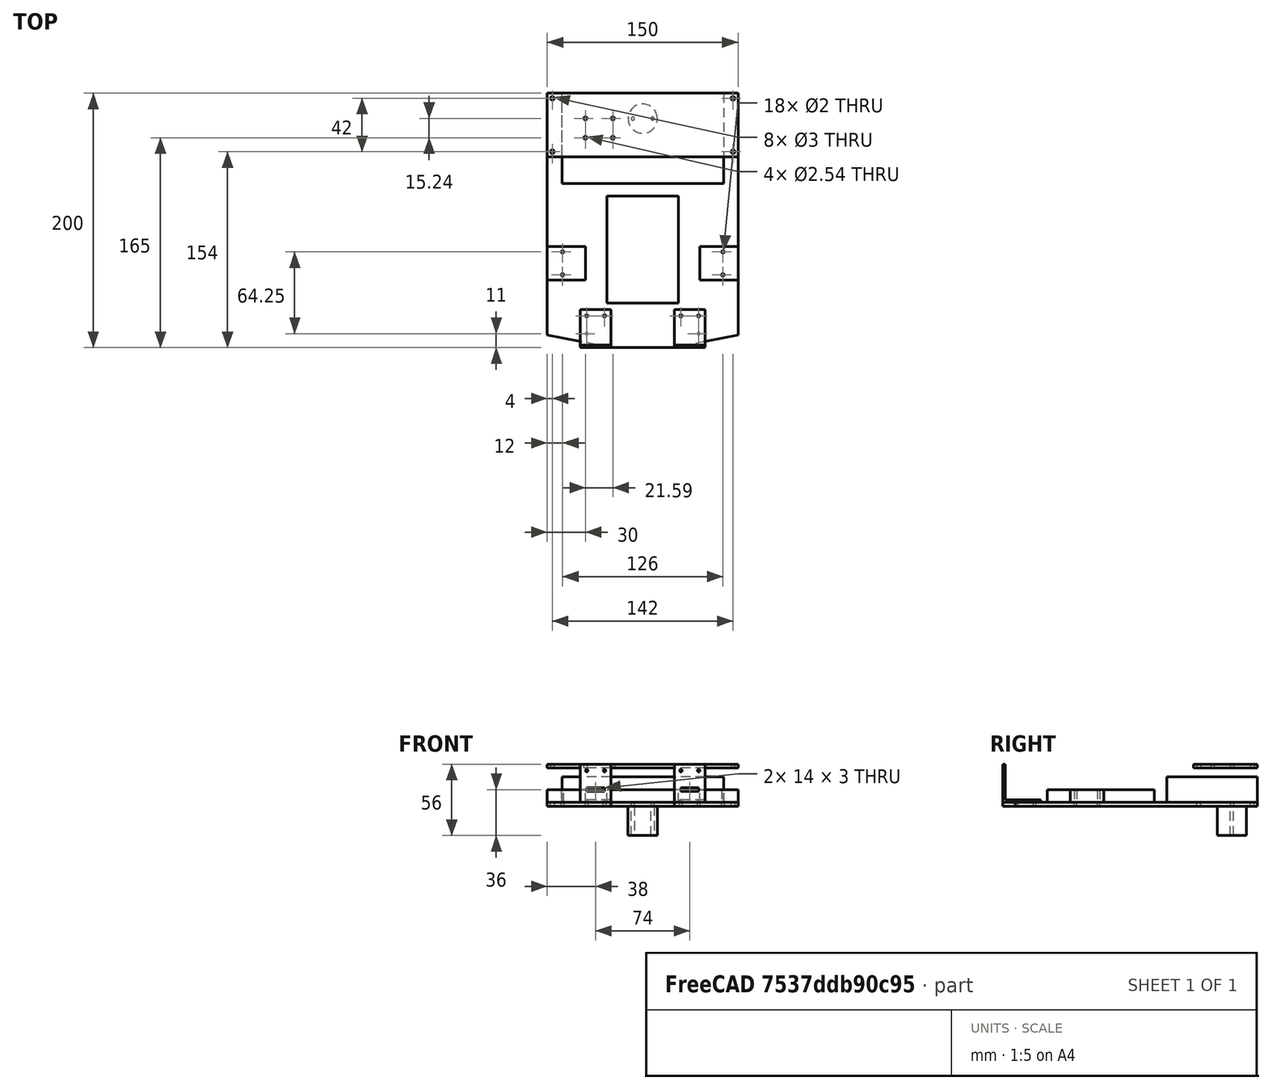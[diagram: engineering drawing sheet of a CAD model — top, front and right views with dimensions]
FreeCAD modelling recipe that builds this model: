
FCSTD DOCUMENT  (FreeCAD 0.20R29177 (Git))
Label: robot
License: All rights reserved
LicenseURL: http://en.wikipedia.org/wiki/All_rights_reserved
objects: TechDraw::DrawViewDimension×62, PartDesign::ShapeBinder×18, PartDesign::Pocket×13, PartDesign::Pad×11, PartDesign::Body×10, TechDraw::DrawProjGroupItem×10, Sketcher::SketchObject×9, TechDraw::DrawSVGTemplate×8, TechDraw::DrawPage×8, TechDraw::DrawProjGroup×7, PartDesign::SubShapeBinder×6, TechDraw::DrawViewAnnotation×3, PartDesign::Fillet×2, App::Part×1
note: 95 computed .brp shape members not serialized (recipe doc carries the construction recipe); baked Part::Feature solids carry a one-line shape summary decoded from their .brp

FEATURE [Sketcher::SketchObject] Sketch  label="ChassisOutline"
  FullyConstrained = true
  MapMode = 5
  Support = -> [XY_Plane]
  sketch-geometry (4):
    g0: LineSegment StartX=-75 StartY=100 StartZ=0 EndX=75 EndY=100 EndZ=0
    g1: LineSegment StartX=75 StartY=100 StartZ=0 EndX=75 EndY=-100 EndZ=0
    g2: LineSegment StartX=75 StartY=-100 StartZ=0 EndX=-75 EndY=-100 EndZ=0
    g3: LineSegment StartX=-75 StartY=-100 StartZ=0 EndX=-75 EndY=100 EndZ=0
  constraints (11):
    c: Coincident(g0,g1)
    c: Coincident(g3,g0)
    c: Horizontal(g0)
    c: Vertical(g1)
    c: Vertical(g3)
    c: Distance(g0) = 150
    c: DistanceY(g2,g0) = 200
    c: Coincident(g2,g1)
    c: Coincident(g2,g3)
    c: Symmetric(g1,g0,g-1)
    c: Horizontal(g2)
FEATURE [Sketcher::SketchObject] Sketch001  label="UpperParts"
  AttachmentOffset = pos=(0,0,3) rot=(0,0,1;0rad)
  ExternalGeometry = -> [Sketch]
  FullyConstrained = true
  MapMode = 5
  Placement = pos=(0,0,3) rot=(0,0,1;0rad)
  Support = -> [XY_Plane]
  sketch-geometry (21):
    g0: LineSegment StartX=-63.5 StartY=100 StartZ=0 EndX=63.5 EndY=100 EndZ=0
    g1: LineSegment StartX=63.5 StartY=100 StartZ=0 EndX=63.5 EndY=29 EndZ=0
    g2: LineSegment StartX=63.5 StartY=29 StartZ=0 EndX=-63.5 EndY=29 EndZ=0
    g3: LineSegment StartX=-63.5 StartY=29 StartZ=0 EndX=-63.5 EndY=100 EndZ=0
    g4: LineSegment StartX=-28 StartY=19 StartZ=0 EndX=28 EndY=19 EndZ=0
    g5: LineSegment StartX=28 StartY=19 StartZ=0 EndX=28 EndY=-65 EndZ=0
    g6: LineSegment StartX=28 StartY=-65 StartZ=0 EndX=-28 EndY=-65 EndZ=0
    g7: LineSegment StartX=-28 StartY=-65 StartZ=0 EndX=-28 EndY=19 EndZ=0
    g8: LineSegment StartX=-75 StartY=-47 StartZ=0 EndX=-45 EndY=-47 EndZ=0
    g9: LineSegment StartX=-45 StartY=-47 StartZ=0 EndX=-45 EndY=-20.5 EndZ=0
    g10: LineSegment StartX=-45 StartY=-20.5 StartZ=0 EndX=-75 EndY=-20.5 EndZ=0
    g11: LineSegment StartX=-75 StartY=-20.5 StartZ=0 EndX=-75 EndY=-47 EndZ=0
    g12: LineSegment StartX=75 StartY=-20.5 StartZ=0 EndX=45 EndY=-20.5 EndZ=0
    g13: LineSegment StartX=45 StartY=-20.5 StartZ=0 EndX=45 EndY=-47 EndZ=0
    g14: LineSegment StartX=45 StartY=-47 StartZ=0 EndX=75 EndY=-47 EndZ=0
    g15: LineSegment StartX=75 StartY=-47 StartZ=0 EndX=75 EndY=-20.5 EndZ=0
    g16: Circle CenterX=-63 CenterY=-24.75 CenterZ=0 NormalX=0 NormalY=0 NormalZ=1 AngleXU=0 Radius=1
    g17: Circle CenterX=-63 CenterY=-42.75 CenterZ=0 NormalX=0 NormalY=0 NormalZ=1 AngleXU=0 Radius=1
    g18: Circle CenterX=63 CenterY=-24.75 CenterZ=0 NormalX=0 NormalY=0 NormalZ=1 AngleXU=0 Radius=1
    g19: Circle CenterX=63 CenterY=-42.75 CenterZ=0 NormalX=0 NormalY=0 NormalZ=1 AngleXU=0 Radius=1
    g20: LineSegment StartX=-45 StartY=-33.75 StartZ=0 EndX=-75 EndY=-33.75 EndZ=0
  constraints (57):
    c: Coincident(g0,g1)
    c: Coincident(g1,g2)
    c: Coincident(g2,g3)
    c: Coincident(g3,g0)
    c: Horizontal(g0)
    c: Vertical(g1)
    c: Vertical(g3)
    c: PointOnObject(g0,g-3)
    c: Coincident(g4,g5)
    c: Coincident(g5,g6)
    c: Coincident(g6,g7)
    c: Coincident(g7,g4)
    c: Horizontal(g6)
    c: Vertical(g5)
    c: Vertical(g7)
    c: Distance(g3) = 71
    c: Distance(g2) = 127
    c: Distance(g6) = 56
    c: Distance(g5) = 84
    c: DistanceY(g4,g2) = 10
    c: Symmetric(g2,g1,g-2)
    c: Symmetric(g4,g4,g-2)
    c: Coincident(g8,g9)
    c: Coincident(g9,g10)
    c: Coincident(g10,g11)
    c: Coincident(g11,g8)
    c: Horizontal(g8)
    c: Horizontal(g10)
    c: Vertical(g9)
    c: Vertical(g11)
    c: PointOnObject(g8,g-4)
    c: Coincident(g12,g13)
    c: Coincident(g13,g14)
    c: Coincident(g14,g15)
    c: Coincident(g15,g12)
    c: Horizontal(g12)
    c: Horizontal(g14)
    c: Vertical(g13)
    c: Vertical(g15)
    c: PointOnObject(g12,g-5)
    c: Equal(g13,g9)
    c: Symmetric(g9,g12,g-2)
    c: DistanceX(g10,g10) = 30
    c: DistanceY(g11,g11) = 26.5
    c: PointOnObject(g20,g9)
    c: PointOnObject(g20,g11)
    c: Symmetric(g10,g8,g20)
    c: Symmetric(g16,g17,g20)
    c: Symmetric(g16,g18,g-2)
    c: Equal(g18,g19)
    c: Equal(g19,g17)
    c: Equal(g17,g16)
    c: Diameter(g16) = 2
    c: DistanceX(g20,g16) = 12
    c: Symmetric(g19,g17,g-2)
    c: DistanceY(g17,g16) = 18
    c: DistanceY(g6,g8) = 18
FEATURE [Sketcher::SketchObject] Sketch002  label="LowerParts"
  ExternalGeometry = -> [Sketch]
  FullyConstrained = true
  MapMode = 5
  Support = -> [XY_Plane]
  sketch-geometry (3):
    g0: Circle CenterX=0 CenterY=80 CenterZ=0 NormalX=0 NormalY=0 NormalZ=1 AngleXU=0 Radius=11.5
    g1: Circle CenterX=-7.75 CenterY=80 CenterZ=0 NormalX=0 NormalY=0 NormalZ=1 AngleXU=0 Radius=1.25
    g2: Circle CenterX=7.75 CenterY=80 CenterZ=0 NormalX=0 NormalY=0 NormalZ=1 AngleXU=0 Radius=1.25
  constraints (8):
    c: PointOnObject(g0,g-2)
    c: Symmetric(g1,g2,g-2)
    c: Horizontal(g0,g1)
    c: Diameter(g2) = 2.5
    c: Equal(g2,g1)
    c: Diameter(g0) = 23
    c: DistanceX(g1,g2) = 15.5
    c: DistanceY(g0,g-3) = 20
FEATURE [PartDesign::ShapeBinder] ShapeBinder
  Support = -> [Sketch,Sketch002,Sketch001]
  TraceSupport = false
FEATURE [PartDesign::Pad] Pad
  Direction = (0,0,1)
  Length = 3
  Length2 = 10
  Profile = -> ShapeBinder
  Type = 0
FEATURE [PartDesign::ShapeBinder] ShapeBinder001
  Support = -> [Sketch001]
  TraceSupport = false
FEATURE [PartDesign::Pocket] Pocket
  BaseFeature = -> Pad
  Direction = (0,0,-1)
  Length = 5
  Length2 = 5
  Profile = -> ShapeBinder001
  Type = 1
FEATURE [PartDesign::ShapeBinder] ShapeBinder002
  Support = -> [Sketch001]
  TraceSupport = false
FEATURE [PartDesign::Pad] Pad001
  Direction = (0,0,1)
  Length = 20
  Length2 = 10
  Profile = -> ShapeBinder002
  Type = 0
FEATURE [PartDesign::Body] Body002  label="BatteryBox"
  Group = -> [ShapeBinder002,Pad001]
  Origin = -> Origin002
  Tip = -> Pad001
FEATURE [PartDesign::ShapeBinder] ShapeBinder003
  Support = -> [Sketch001]
  TraceSupport = false
FEATURE [PartDesign::Pad] Pad002
  Direction = (0,0,1)
  Length = 10
  Length2 = 10
  Profile = -> ShapeBinder003
  Type = 0
FEATURE [PartDesign::Body] Body003  label="Breadboard"
  Group = -> [ShapeBinder003,Pad002]
  Origin = -> Origin003
  Tip = -> Pad002
FEATURE [PartDesign::ShapeBinder] ShapeBinder004
  Support = -> [Sketch001]
  TraceSupport = false
FEATURE [PartDesign::Pad] Pad003
  Direction = (0,0,1)
  Length = 10
  Length2 = 10
  Profile = -> ShapeBinder004
  Type = 0
FEATURE [PartDesign::Body] Body004  label="LeftMotor"
  Group = -> [ShapeBinder004,Pad003]
  Origin = -> Origin004
  Tip = -> Pad003
FEATURE [PartDesign::ShapeBinder] ShapeBinder005
  Support = -> [Sketch001]
  TraceSupport = false
FEATURE [PartDesign::Pad] Pad004
  Direction = (0,0,1)
  Length = 10
  Length2 = 10
  Profile = -> ShapeBinder005
  Type = 0
FEATURE [PartDesign::Body] Body005  label="RightMotor"
  Group = -> [ShapeBinder005,Pad004]
  Origin = -> Origin005
  Tip = -> Pad004
FEATURE [PartDesign::ShapeBinder] ShapeBinder006
  Support = -> [Sketch001]
  TraceSupport = false
FEATURE [PartDesign::Pocket] Pocket001
  BaseFeature = -> Pocket
  Direction = (0,0,-1)
  Length = 5
  Length2 = 5
  Profile = -> ShapeBinder006
  Type = 1
FEATURE [PartDesign::ShapeBinder] ShapeBinder007
  Support = -> [Sketch002]
  TraceSupport = false
FEATURE [PartDesign::Pocket] Pocket002
  BaseFeature = -> Pocket001
  Direction = (0,0,-1)
  Length = 5
  Length2 = 5
  Profile = -> ShapeBinder007
  Reversed = true
  Type = 1
FEATURE [PartDesign::ShapeBinder] ShapeBinder008
  Support = -> [Sketch002]
  TraceSupport = false
FEATURE [PartDesign::Pad] Pad005
  Direction = (0,0,1)
  Length = 23
  Length2 = 10
  Profile = -> ShapeBinder008
  Reversed = true
  Type = 0
FEATURE [PartDesign::Body] Body006  label="Castor"
  Group = -> [ShapeBinder008,Pad005]
  Origin = -> Origin006
  Tip = -> Pad005
FEATURE [TechDraw::DrawSVGTemplate] Template
  Height = 297
  Orientation = 0
  Width = 210
FEATURE [Sketcher::SketchObject] Sketch003  label="BevelFront"
  ExternalGeometry = -> [Sketch]
  FullyConstrained = true
  MapMode = 5
  Support = -> [XY_Plane]
  sketch-geometry (6):
    g0: LineSegment StartX=-75 StartY=-90 StartZ=0 EndX=-25 EndY=-100 EndZ=0
    g1: LineSegment StartX=25 StartY=-100 StartZ=0 EndX=75 EndY=-90 EndZ=0
    g2: LineSegment StartX=-75 StartY=-90 StartZ=0 EndX=-75 EndY=-100 EndZ=0
    g3: LineSegment StartX=-25 StartY=-100 StartZ=0 EndX=-75 EndY=-100 EndZ=0
    g4: LineSegment StartX=25 StartY=-100 StartZ=0 EndX=75 EndY=-100 EndZ=0
    g5: LineSegment StartX=75 StartY=-100 StartZ=0 EndX=75 EndY=-90 EndZ=0
  constraints (14):
    c: PointOnObject(g0,g-4)
    c: PointOnObject(g0,g-3)
    c: Symmetric(g1,g0,g-2)
    c: Symmetric(g0,g1,g-2)
    c: DistanceY(g-4,g0) = 10
    c: DistanceX(g0,g1) = 50
    c: Coincident(g2,g0)
    c: Coincident(g2,g-4)
    c: Coincident(g3,g2)
    c: Coincident(g3,g0)
    c: Coincident(g1,g4)
    c: Coincident(g4,g-5)
    c: Coincident(g4,g5)
    c: Coincident(g5,g1)
FEATURE [PartDesign::ShapeBinder] ShapeBinder009
  Support = -> [Sketch003]
  TraceSupport = false
FEATURE [PartDesign::Pocket] Pocket003
  BaseFeature = -> Pocket002
  Direction = (0,0,-1)
  Length = 5
  Length2 = 5
  Profile = -> ShapeBinder009
  Reversed = true
  Type = 1
FEATURE [PartDesign::ShapeBinder] ShapeBinder010
  Support = -> [Sketch003]
  TraceSupport = false
FEATURE [PartDesign::Pocket] Pocket004
  BaseFeature = -> Pocket003
  Direction = (0,0,-1)
  Length = 5
  Length2 = 5
  Profile = -> ShapeBinder010
  Reversed = true
  Type = 1
FEATURE [TechDraw::DrawSVGTemplate] Template001
  Height = 297
  Orientation = 0
  Width = 210
FEATURE [TechDraw::DrawProjGroupItem] ProjItem001  label="Front001"
  CoarseView = false
  Direction = (0,0,1)
  Focus = 100
  HardHidden = false
  IsoCount = 0
  IsoHidden = false
  IsoVisible = false
  LockPosition = true
  Perspective = false
  Rotation = 0
  RotationVector = (-1,0,0)
  ScaleType = 2
  SeamHidden = false
  SeamVisible = true
  SmoothHidden = false
  SmoothVisible = true
  Source = -> [Pocket002]
  Type = 0
  X = 0
  XDirection = (-1,0,0)
  Y = 0
FEATURE [TechDraw::DrawProjGroup] ProjGroup001
  Anchor = -> ProjItem001
  AutoDistribute = true
  LockPosition = false
  ProjectionType = 0
  Rotation = 0
  ScaleType = 0
  Source = -> [Pocket002]
  Views = -> [ProjItem001]
  X = 105
  Y = 148.5
  spacingX = 15
  spacingY = 15
FEATURE [TechDraw::DrawViewDimension] Dimension012
  AngleOverride = false
  Arbitrary = false
  ArbitraryTolerances = false
  EqualTolerance = true
  ExtensionAngle = 0
  FormatSpec = ⌀%.2f
  FormatSpecOverTolerance = %+.2f
  FormatSpecUnderTolerance = %+.2f
  Inverted = false
  LineAngle = 0
  LockPosition = false
  MeasureType = 1
  OverTolerance = 0
  References2D = -> [ProjItem001]
  Rotation = 0
  ScaleType = 0
  TheoreticalExact = false
  Type = 5
  UnderTolerance = 0
  X = 45.3924
  Y = 74.404
FEATURE [TechDraw::DrawViewDimension] Dimension013
  AngleOverride = false
  Arbitrary = false
  ArbitraryTolerances = false
  EqualTolerance = true
  ExtensionAngle = 0
  FormatSpec = ⌀%.2f
  FormatSpecOverTolerance = %+.2f
  FormatSpecUnderTolerance = %+.2f
  Inverted = false
  LineAngle = 0
  LockPosition = false
  MeasureType = 1
  OverTolerance = 0
  References2D = -> [ProjItem001]
  Rotation = 0
  ScaleType = 0
  TheoreticalExact = false
  Type = 5
  UnderTolerance = 0
  X = 22.3571
  Y = -61.4242
FEATURE [TechDraw::DrawPage] Page001  label="ChassisWithoutBevelsAllDimensions"
  KeepUpdated = true
  NextBalloonIndex = 1
  ProjectionType = 0
  Template = -> Template001
  Views = -> [ProjGroup001,Dimension012,Dimension013]
FEATURE [TechDraw::DrawSVGTemplate] Template002
  Height = 297
  Orientation = 0
  Width = 210
FEATURE [Sketcher::SketchObject] Sketch004  label="DaughterCardOutline"
  AttachmentOffset = pos=(0,0,30) rot=(0,0,1;0rad)
  ExternalGeometry = -> [Sketch]
  FullyConstrained = true
  MapMode = 5
  Placement = pos=(0,0,30) rot=(0,0,1;0rad)
  Support = -> [XY_Plane]
  sketch-geometry (8):
    g0: LineSegment StartX=-75 StartY=100 StartZ=0 EndX=75 EndY=100 EndZ=0
    g1: LineSegment StartX=75 StartY=100 StartZ=0 EndX=75 EndY=50 EndZ=0
    g2: LineSegment StartX=75 StartY=50 StartZ=0 EndX=-75 EndY=50 EndZ=0
    g3: LineSegment StartX=-75 StartY=50 StartZ=0 EndX=-75 EndY=100 EndZ=0
    g4: Circle CenterX=-71 CenterY=96 CenterZ=0 NormalX=0 NormalY=0 NormalZ=1 AngleXU=0 Radius=1.5
    g5: Circle CenterX=-71 CenterY=54 CenterZ=0 NormalX=0 NormalY=0 NormalZ=1 AngleXU=0 Radius=1.5
    g6: Circle CenterX=71 CenterY=96 CenterZ=0 NormalX=0 NormalY=0 NormalZ=1 AngleXU=0 Radius=1.5
    g7: Circle CenterX=71 CenterY=54 CenterZ=0 NormalX=0 NormalY=0 NormalZ=1 AngleXU=0 Radius=1.5
  constraints (22):
    c: Coincident(g0,g1)
    c: Coincident(g1,g2)
    c: Coincident(g2,g3)
    c: Coincident(g3,g0)
    c: Horizontal(g0)
    c: Horizontal(g2)
    c: Vertical(g1)
    c: Vertical(g3)
    c: Coincident(g0,g-4)
    c: PointOnObject(g1,g-5)
    c: DistanceY(g3,g3) = 50
    c: DistanceY(g4,g0) = 4
    c: DistanceX(g0,g4) = 4
    c: Vertical(g5,g4)
    c: Horizontal(g5,g7)
    c: Equal(g6,g4)
    c: Equal(g4,g5)
    c: Equal(g5,g7)
    c: Diameter(g6) = 3
    c: Vertical(g6,g7)
    c: Symmetric(g4,g6,g-2)
    c: DistanceY(g2,g5) = 4
FEATURE [PartDesign::ShapeBinder] ShapeBinder011
  Support = -> [Sketch004]
  TraceSupport = false
FEATURE [PartDesign::Pocket] Pocket005
  BaseFeature = -> Pocket004
  Direction = (0,0,-1)
  Length = 5
  Length2 = 5
  Profile = -> ShapeBinder011
  Reversed = true
  Type = 1
FEATURE [PartDesign::ShapeBinder] ShapeBinder012
  Support = -> [Sketch004]
  TraceSupport = false
FEATURE [PartDesign::Pad] Pad006
  Direction = (0,0,1)
  Length = 3
  Length2 = 10
  Profile = -> ShapeBinder012
  Type = 0
FEATURE [TechDraw::DrawSVGTemplate] Template003
  Height = 297
  Orientation = 0
  Width = 210
FEATURE [App::Part] Part
  Origin = -> Origin008
FEATURE [Sketcher::SketchObject] Sketch005  label="SensorBracketBase"
  AttachmentOffset = pos=(0,0,3) rot=(0,0,1;0rad)
  ExternalGeometry = -> [Sketch]
  FullyConstrained = true
  MapMode = 5
  Placement = pos=(0,0,3) rot=(0,0,1;0rad)
  Support = -> [XY_Plane]
  sketch-geometry (13):
    g0: LineSegment StartX=-49 StartY=-100 StartZ=0 EndX=-25 EndY=-100 EndZ=0
    g1: LineSegment StartX=-25 StartY=-100 StartZ=0 EndX=-25 EndY=-70 EndZ=0
    g2: LineSegment StartX=-25 StartY=-70 StartZ=0 EndX=-49 EndY=-70 EndZ=0
    g3: LineSegment StartX=-49 StartY=-70 StartZ=0 EndX=-49 EndY=-100 EndZ=0
    g4: LineSegment StartX=25 StartY=-100 StartZ=0 EndX=49 EndY=-100 EndZ=0
    g5: LineSegment StartX=49 StartY=-100 StartZ=0 EndX=49 EndY=-70 EndZ=0
    g6: LineSegment StartX=49 StartY=-70 StartZ=0 EndX=25 EndY=-70 EndZ=0
    g7: LineSegment StartX=25 StartY=-70 StartZ=0 EndX=25 EndY=-100 EndZ=0
    g8: Circle CenterX=-30 CenterY=-75 CenterZ=0 NormalX=0 NormalY=0 NormalZ=1 AngleXU=0 Radius=1
    g9: Circle CenterX=-44 CenterY=-75 CenterZ=0 NormalX=0 NormalY=0 NormalZ=1 AngleXU=0 Radius=1
    g10: Circle CenterX=30 CenterY=-75 CenterZ=0 NormalX=0 NormalY=0 NormalZ=1 AngleXU=0 Radius=1
    g11: Circle CenterX=44 CenterY=-75 CenterZ=0 NormalX=0 NormalY=0 NormalZ=1 AngleXU=0 Radius=1
    g12: LineSegment StartX=-37 StartY=-70 StartZ=0 EndX=-37 EndY=-100 EndZ=0
  constraints (35):
    c: Coincident(g0,g1)
    c: Coincident(g1,g2)
    c: Coincident(g2,g3)
    c: Coincident(g3,g0)
    c: Horizontal(g0)
    c: Horizontal(g2)
    c: Vertical(g1)
    c: Vertical(g3)
    c: PointOnObject(g0,g-3)
    c: Coincident(g4,g5)
    c: Coincident(g5,g6)
    c: Coincident(g6,g7)
    c: Coincident(g7,g4)
    c: Horizontal(g4)
    c: Horizontal(g6)
    c: Vertical(g5)
    c: Vertical(g7)
    c: PointOnObject(g4,g-3)
    c: DistanceY(g1,g1) = 30
    c: Equal(g2,g6)
    c: Symmetric(g1,g6,g-2)
    c: DistanceX(g2,g2) = 24
    c: DistanceX(g0,g4) = 50
    c: PointOnObject(g12,g2)
    c: PointOnObject(g12,g0)
    c: Symmetric(g2,g1,g12)
    c: Symmetric(g9,g8,g12)
    c: Symmetric(g8,g10,g-2)
    c: Symmetric(g11,g9,g-2)
    c: Equal(g9,g8)
    c: Equal(g8,g10)
    c: Equal(g10,g11)
    c: Diameter(g9) = 2
    c: DistanceX(g9,g8) = 14
    c: DistanceY(g9,g2) = 5
FEATURE [PartDesign::ShapeBinder] ShapeBinder013
  Support = -> [Sketch005]
  TraceSupport = false
FEATURE [PartDesign::Pad] Pad007
  Direction = (0,0,1)
  Length = 2
  Length2 = 10
  Profile = -> ShapeBinder013
  Type = 0
FEATURE [PartDesign::ShapeBinder] ShapeBinder014
  Support = -> [Sketch005]
  TraceSupport = false
FEATURE [PartDesign::Pad] Pad008
  Direction = (0,0,1)
  Length = 2
  Length2 = 10
  Profile = -> ShapeBinder014
  Type = 0
FEATURE [Sketcher::SketchObject] Sketch007  label="SensorBracketFront"
  AttachmentOffset = pos=(0,0,100) rot=(0,0,1;0rad)
  ExternalGeometry = -> [Sketch005]
  FullyConstrained = true
  MapMode = 5
  Placement = pos=(0,-100,-2.22e-14) rot=(1,0,0;1.5708rad)
  Support = -> [XZ_Plane]
  sketch-geometry (21):
    g0: LineSegment StartX=-49 StartY=3 StartZ=0 EndX=-25 EndY=3 EndZ=0
    g1: LineSegment StartX=-25 StartY=3 StartZ=0 EndX=-25 EndY=33 EndZ=0
    g2: LineSegment StartX=-25 StartY=33 StartZ=0 EndX=-49 EndY=33 EndZ=0
    g3: LineSegment StartX=-49 StartY=33 StartZ=0 EndX=-49 EndY=3 EndZ=0
    g4: LineSegment StartX=-37 StartY=33 StartZ=0 EndX=-37 EndY=3 EndZ=0
    g5: Circle CenterX=-44 CenterY=28 CenterZ=0 NormalX=0 NormalY=0 NormalZ=1 AngleXU=0 Radius=1
    g6: Circle CenterX=-30 CenterY=28 CenterZ=0 NormalX=0 NormalY=0 NormalZ=1 AngleXU=0 Radius=1
    g7: LineSegment StartX=25 StartY=3 StartZ=0 EndX=49 EndY=3 EndZ=0
    g8: LineSegment StartX=49 StartY=3 StartZ=0 EndX=49 EndY=33 EndZ=0
    g9: LineSegment StartX=49 StartY=33 StartZ=0 EndX=25 EndY=33 EndZ=0
    g10: LineSegment StartX=25 StartY=33 StartZ=0 EndX=25 EndY=3 EndZ=0
    g11: Circle CenterX=30 CenterY=28 CenterZ=0 NormalX=0 NormalY=0 NormalZ=1 AngleXU=0 Radius=1
    g12: Circle CenterX=44 CenterY=28 CenterZ=0 NormalX=0 NormalY=0 NormalZ=1 AngleXU=0 Radius=1
    g13: LineSegment StartX=-44 StartY=11.5 StartZ=0 EndX=-30 EndY=11.5 EndZ=0
    g14: LineSegment StartX=-30 StartY=11.5 StartZ=0 EndX=-30 EndY=14.5 EndZ=0
    g15: LineSegment StartX=-30 StartY=14.5 StartZ=0 EndX=-44 EndY=14.5 EndZ=0
    g16: LineSegment StartX=-44 StartY=14.5 StartZ=0 EndX=-44 EndY=11.5 EndZ=0
    g17: LineSegment StartX=30 StartY=14.5 StartZ=0 EndX=44 EndY=14.5 EndZ=0
    g18: LineSegment StartX=44 StartY=14.5 StartZ=0 EndX=44 EndY=11.5 EndZ=0
    g19: LineSegment StartX=44 StartY=11.5 StartZ=0 EndX=30 EndY=11.5 EndZ=0
    g20: LineSegment StartX=30 StartY=11.5 StartZ=0 EndX=30 EndY=14.5 EndZ=0
  constraints (53):
    c: Coincident(g0,g1)
    c: Coincident(g1,g2)
    c: Coincident(g2,g3)
    c: Coincident(g3,g0)
    c: Horizontal(g2)
    c: Vertical(g1)
    c: Vertical(g3)
    c: Coincident(g0,g-3)
    c: Coincident(g0,g-3)
    c: DistanceY(g3,g3) = 30
    c: PointOnObject(g4,g2)
    c: PointOnObject(g4,g0)
    c: Symmetric(g1,g2,g4)
    c: Coincident(g7,g8)
    c: Coincident(g8,g9)
    c: Coincident(g9,g10)
    c: Coincident(g10,g7)
    c: Horizontal(g9)
    c: Vertical(g8)
    c: Vertical(g10)
    c: Coincident(g7,g-4)
    c: Coincident(g7,g-4)
    c: Equal(g1,g10)
    c: Symmetric(g12,g5,g-2)
    c: Symmetric(g6,g11,g-2)
    c: Equal(g5,g6)
    c: Equal(g6,g11)
    c: Equal(g11,g12)
    c: Symmetric(g6,g5,g4)
    c: Diameter(g5) = 2
    c: DistanceX(g5,g6) = 14
    c: DistanceY(g5,g2) = 5
    c: Coincident(g13,g14)
    c: Coincident(g14,g15)
    c: Coincident(g15,g16)
    c: Coincident(g16,g13)
    c: Horizontal(g15)
    c: Vertical(g14)
    c: Vertical(g16)
    c: Symmetric(g13,g13,g4)
    c: DistanceX(g13,g13) = 14
    c: DistanceY(g13,g6) = 16.5
    c: DistanceY(g14,g14) = 3
    c: Coincident(g17,g18)
    c: Coincident(g18,g19)
    c: Coincident(g19,g20)
    c: Coincident(g20,g17)
    c: Horizontal(g17)
    c: Horizontal(g19)
    c: Vertical(g18)
    c: Vertical(g20)
    c: Symmetric(g17,g14,g-2)
    c: Symmetric(g13,g18,g-2)
FEATURE [PartDesign::ShapeBinder] ShapeBinder015
  Support = -> [Sketch007]
  TraceSupport = false
FEATURE [PartDesign::Pad] Pad009
  BaseFeature = -> Pad007
  Direction = (0,1,4e-16)
  Length = 2
  Length2 = 10
  Profile = -> ShapeBinder015
  Type = 0
FEATURE [PartDesign::SubShapeBinder] Binder
  BindCopyOnChange = 0
  BindMode = 0
  ClaimChildren = false
  Context = -> Body009 [Binder.]
  Fuse = false
  MakeFace = true
  OffsetFill = false
  OffsetIntersection = false
  OffsetJoinType = 0
  OffsetOpenResult = false
  PartialLoad = false
  Relative = true
  Support = -> [Body[Sketch007.Edge11,Sketch007.Edge12,Sketch007.Edge9,Sketch007.Edge10,Sketch007.Edge8,Sketch007.Edge7]]
  _Version = 2
FEATURE [PartDesign::Pad] Pad010
  BaseFeature = -> Pad008
  Direction = (0,1,4e-16)
  Length = 2
  Length2 = 10
  Profile = -> Binder
  Type = 0
FEATURE [PartDesign::SubShapeBinder] Binder001
  BindCopyOnChange = 0
  BindMode = 0
  ClaimChildren = false
  Context = -> Body008 [Binder001.]
  Fuse = false
  MakeFace = true
  OffsetFill = false
  OffsetIntersection = false
  OffsetJoinType = 0
  OffsetOpenResult = false
  PartialLoad = false
  Relative = true
  Support = -> [Body[Sketch007.Edge15,Sketch007.Edge16,Sketch007.Edge13,Sketch007.Edge14]]
  _Version = 2
FEATURE [PartDesign::Pocket] Pocket006
  BaseFeature = -> Pad009
  Direction = (0,-1,0)
  Length = 5
  Length2 = 5
  Profile = -> Binder001
  Reversed = true
  Type = 1
FEATURE [PartDesign::SubShapeBinder] Binder002
  BindCopyOnChange = 0
  BindMode = 0
  ClaimChildren = false
  Context = -> Body009 [Binder002.]
  Fuse = false
  MakeFace = true
  OffsetFill = false
  OffsetIntersection = false
  OffsetJoinType = 0
  OffsetOpenResult = false
  PartialLoad = false
  Relative = true
  Support = -> [Body[Sketch007.Edge17,Sketch007.Edge20,Sketch007.Edge19,Sketch007.Edge18]]
  _Version = 2
FEATURE [PartDesign::Pocket] Pocket007
  BaseFeature = -> Pad010
  Direction = (0,-1,0)
  Length = 5
  Length2 = 5
  Profile = -> Binder002
  Reversed = true
  Type = 1
FEATURE [PartDesign::SubShapeBinder] Binder003
  BindCopyOnChange = 0
  BindMode = 0
  ClaimChildren = false
  Context = -> Body001 [Binder003.]
  Fuse = false
  MakeFace = true
  OffsetFill = false
  OffsetIntersection = false
  OffsetJoinType = 0
  OffsetOpenResult = false
  PartialLoad = false
  Relative = true
  Support = -> [Body[Sketch005.Edge10,Sketch005.Edge9]]
  _Version = 2
FEATURE [PartDesign::Pocket] Pocket008
  BaseFeature = -> Pocket005
  Direction = (0,0,-1)
  Length = 5
  Length2 = 5
  Profile = -> Binder003
  Type = 1
FEATURE [PartDesign::SubShapeBinder] Binder004
  BindCopyOnChange = 0
  BindMode = 0
  ClaimChildren = false
  Context = -> Body001 [Binder004.]
  Fuse = false
  MakeFace = true
  OffsetFill = false
  OffsetIntersection = false
  OffsetJoinType = 0
  OffsetOpenResult = false
  PartialLoad = false
  Relative = true
  Support = -> [Body[Sketch005.Edge11,Sketch005.Edge12]]
  _Version = 2
FEATURE [PartDesign::Pocket] Pocket009
  BaseFeature = -> Pocket008
  Direction = (0,0,-1)
  Length = 5
  Length2 = 5
  Profile = -> Binder004
  Type = 1
FEATURE [PartDesign::SubShapeBinder] Binder005
  BindCopyOnChange = 0
  BindMode = 0
  ClaimChildren = false
  Context = -> Body001 [Binder005.]
  Fuse = false
  MakeFace = true
  OffsetFill = false
  OffsetIntersection = false
  OffsetJoinType = 0
  OffsetOpenResult = false
  PartialLoad = false
  Relative = true
  Support = -> [Body[Sketch004.Edge5,Sketch004.Edge6,Sketch004.Edge8,Sketch004.Vertex7,Sketch004.Edge7]]
  _Version = 2
FEATURE [PartDesign::Pocket] Pocket010
  BaseFeature = -> Pocket009
  Direction = (0,0,-1)
  Length = 5
  Length2 = 5
  Profile = -> Binder005
  Type = 1
FEATURE [TechDraw::DrawSVGTemplate] Template004
  Height = 297
  Orientation = 0
  Width = 210
FEATURE [PartDesign::Fillet] Fillet
  Base = -> Pocket006 [Edge21]
  BaseFeature = -> Pocket006
  Radius = 1
  SupportTransform = false
  UseAllEdges = false
FEATURE [PartDesign::Body] Body008  label="LeftSensorBracket"
  Group = -> [ShapeBinder013,Pad007,ShapeBinder015,Pad009,Binder001,Pocket006,Fillet]
  Origin = -> Origin009
  Tip = -> Fillet
FEATURE [TechDraw::DrawProjGroupItem] ProjItem004  label="Front004"
  CoarseView = false
  Direction = (0,-1,0)
  Focus = 100
  HardHidden = false
  IsoCount = 0
  IsoHidden = false
  IsoVisible = false
  LockPosition = true
  Perspective = false
  Rotation = 0
  RotationVector = (1,0,0)
  Scale = 1.5
  ScaleType = 2
  SeamHidden = false
  SeamVisible = true
  SmoothHidden = false
  SmoothVisible = true
  Source = -> [Body008]
  Type = 0
  X = 0
  XDirection = (1,0,0)
  Y = 0
FEATURE [TechDraw::DrawProjGroupItem] ProjItem005  label="FrontTopRight"
  CoarseView = false
  Direction = (0.57735,-0.57735,0.57735)
  Focus = 100
  HardHidden = false
  IsoCount = 0
  IsoHidden = false
  IsoVisible = false
  LockPosition = false
  Perspective = false
  Rotation = 0
  RotationVector = (1,0,0)
  Scale = 1.5
  ScaleType = 2
  SeamHidden = false
  SeamVisible = true
  SmoothHidden = false
  SmoothVisible = true
  Source = -> [Body008]
  Type = 7
  X = -72.2756
  XDirection = (0.707107,0.707107,0)
  Y = -74.8154
FEATURE [TechDraw::DrawProjGroupItem] ProjItem006  label="Right"
  CoarseView = false
  Direction = (1,-1e-16,0)
  Focus = 100
  HardHidden = false
  IsoCount = 0
  IsoHidden = false
  IsoVisible = false
  LockPosition = false
  Perspective = false
  Rotation = 0
  RotationVector = (1,0,0)
  Scale = 1.5
  ScaleType = 2
  SeamHidden = false
  SeamVisible = true
  SmoothHidden = false
  SmoothVisible = true
  Source = -> [Body008]
  Type = 2
  X = -66.1378
  XDirection = (1e-16,1,0)
  Y = 0
FEATURE [PartDesign::Fillet] Fillet001
  Base = -> Pocket007 [Edge21]
  BaseFeature = -> Pocket007
  Radius = 1
  SupportTransform = false
  UseAllEdges = false
FEATURE [PartDesign::Body] Body009  label="RightSensorBracket"
  Group = -> [ShapeBinder014,Pad008,Binder,Pad010,Binder002,Pocket007,Fillet001]
  Origin = -> Origin010
  Tip = -> Fillet001
FEATURE [TechDraw::DrawViewDimension] Dimension033
  AngleOverride = false
  Arbitrary = false
  ArbitraryTolerances = false
  EqualTolerance = true
  ExtensionAngle = 0
  FormatSpec = %.2f
  FormatSpecOverTolerance = %+.2f
  FormatSpecUnderTolerance = %+.2f
  Inverted = false
  LineAngle = 0
  LockPosition = false
  MeasureType = 1
  OverTolerance = 0
  References2D = -> [ProjItem004]
  Rotation = 0
  ScaleType = 0
  TheoreticalExact = false
  Type = 1
  UnderTolerance = 0
  X = -2.05098
  Y = 34.5712
FEATURE [TechDraw::DrawViewDimension] Dimension034
  AngleOverride = false
  Arbitrary = false
  ArbitraryTolerances = false
  EqualTolerance = true
  ExtensionAngle = 0
  FormatSpec = %.2f
  FormatSpecOverTolerance = %+.2f
  FormatSpecUnderTolerance = %+.2f
  Inverted = false
  LineAngle = 0
  LockPosition = false
  MeasureType = 1
  OverTolerance = 0
  References2D = -> [ProjItem004]
  Rotation = 0
  ScaleType = 0
  TheoreticalExact = false
  Type = 1
  UnderTolerance = 0
  X = 0
  Y = 0.668294
FEATURE [TechDraw::DrawViewDimension] Dimension035
  AngleOverride = false
  Arbitrary = false
  ArbitraryTolerances = false
  EqualTolerance = true
  ExtensionAngle = 0
  FormatSpec = %.2f
  FormatSpecOverTolerance = %+.2f
  FormatSpecUnderTolerance = %+.2f
  Inverted = false
  LineAngle = 0
  LockPosition = false
  MeasureType = 1
  OverTolerance = 0
  References2D = -> [ProjItem004]
  Rotation = 0
  ScaleType = 0
  TheoreticalExact = false
  Type = 1
  UnderTolerance = 0
  X = 0.341829
  Y = 19.7781
FEATURE [TechDraw::DrawViewDimension] Dimension036
  AngleOverride = false
  Arbitrary = false
  ArbitraryTolerances = false
  EqualTolerance = true
  ExtensionAngle = 0
  FormatSpec = %.2f
  FormatSpecOverTolerance = %+.2f
  FormatSpecUnderTolerance = %+.2f
  Inverted = false
  LineAngle = 0
  LockPosition = false
  MeasureType = 1
  OverTolerance = 0
  References2D = -> [ProjItem004]
  Rotation = 0
  ScaleType = 0
  TheoreticalExact = false
  Type = 2
  UnderTolerance = 0
  X = -22.5787
  Y = 18.8572
FEATURE [TechDraw::DrawViewDimension] Dimension037
  AngleOverride = false
  Arbitrary = false
  ArbitraryTolerances = false
  EqualTolerance = true
  ExtensionAngle = 0
  FormatSpec = %.2f
  FormatSpecOverTolerance = %+.2f
  FormatSpecUnderTolerance = %+.2f
  Inverted = false
  LineAngle = 0
  LockPosition = false
  MeasureType = 1
  OverTolerance = 0
  References2D = -> [ProjItem004]
  Rotation = 0
  ScaleType = 0
  TheoreticalExact = false
  Type = 1
  UnderTolerance = 0
  X = -14.0107
  Y = 8.70284
FEATURE [TechDraw::DrawViewDimension] Dimension038
  AngleOverride = false
  Arbitrary = false
  ArbitraryTolerances = false
  EqualTolerance = true
  ExtensionAngle = 0
  FormatSpec = %.2f
  FormatSpecOverTolerance = %+.2f
  FormatSpecUnderTolerance = %+.2f
  Inverted = false
  LineAngle = 0
  LockPosition = false
  MeasureType = 1
  OverTolerance = 0
  References2D = -> [ProjItem004]
  Rotation = 0
  ScaleType = 0
  TheoreticalExact = false
  Type = 2
  UnderTolerance = 0
  X = 13.4739
  Y = -13.9774
FEATURE [TechDraw::DrawViewDimension] Dimension039
  AngleOverride = false
  Arbitrary = false
  ArbitraryTolerances = false
  EqualTolerance = true
  ExtensionAngle = 0
  FormatSpec = %.2f
  FormatSpecOverTolerance = %+.2f
  FormatSpecUnderTolerance = %+.2f
  Inverted = false
  LineAngle = 0
  LockPosition = false
  MeasureType = 1
  OverTolerance = 0
  References2D = -> [ProjItem004]
  Rotation = 0
  ScaleType = 0
  TheoreticalExact = false
  Type = 2
  UnderTolerance = 0
  X = -29.1725
  Y = 4.39281
FEATURE [TechDraw::DrawProjGroupItem] ProjItem007  label="Top"
  CoarseView = false
  Direction = (0,0,1)
  Focus = 100
  HardHidden = false
  IsoCount = 0
  IsoHidden = false
  IsoVisible = false
  LockPosition = false
  Perspective = false
  Rotation = 0
  RotationVector = (1,0,0)
  Scale = 1.5
  ScaleType = 2
  SeamHidden = false
  SeamVisible = true
  SmoothHidden = false
  SmoothVisible = true
  Source = -> [Body008]
  Type = 4
  X = 0
  XDirection = (1,0,0)
  Y = -78.4135
FEATURE [TechDraw::DrawProjGroup] ProjGroup004
  Anchor = -> ProjItem004
  AutoDistribute = true
  LockPosition = false
  ProjectionType = 0
  Rotation = 0
  Scale = 1.5
  ScaleType = 1
  Source = -> [Body008]
  Views = -> [ProjItem004,ProjItem005,ProjItem006,ProjItem007]
  X = 141.302
  Y = 167.779
  spacingX = 15
  spacingY = 15
FEATURE [TechDraw::DrawViewDimension] Dimension040
  AngleOverride = false
  Arbitrary = false
  ArbitraryTolerances = false
  EqualTolerance = true
  ExtensionAngle = 0
  FormatSpec = %.2f
  FormatSpecOverTolerance = %+.2f
  FormatSpecUnderTolerance = %+.2f
  Inverted = false
  LineAngle = 0
  LockPosition = false
  MeasureType = 1
  OverTolerance = 0
  References2D = -> [ProjItem007]
  Rotation = 0
  ScaleType = 0
  TheoreticalExact = false
  Type = 1
  UnderTolerance = 0
  X = -1.70915
  Y = 1.01572
FEATURE [TechDraw::DrawViewDimension] Dimension041
  AngleOverride = false
  Arbitrary = false
  ArbitraryTolerances = false
  EqualTolerance = true
  ExtensionAngle = 0
  FormatSpec = %.2f
  FormatSpecOverTolerance = %+.2f
  FormatSpecUnderTolerance = %+.2f
  Inverted = false
  LineAngle = 0
  LockPosition = false
  MeasureType = 1
  OverTolerance = 0
  References2D = -> [ProjItem007]
  Rotation = 0
  ScaleType = 0
  TheoreticalExact = false
  Type = 2
  UnderTolerance = 0
  X = -22.8951
  Y = 18.5281
FEATURE [TechDraw::DrawViewDimension] Dimension042
  AngleOverride = false
  Arbitrary = false
  ArbitraryTolerances = false
  EqualTolerance = true
  ExtensionAngle = 0
  FormatSpec = %.2f
  FormatSpecOverTolerance = %+.2f
  FormatSpecUnderTolerance = %+.2f
  Inverted = false
  LineAngle = 0
  LockPosition = false
  MeasureType = 1
  OverTolerance = 0
  References2D = -> [ProjItem007]
  Rotation = 0
  ScaleType = 0
  TheoreticalExact = false
  Type = 1
  UnderTolerance = 0
  X = -14.5918
  Y = 35.0277
FEATURE [TechDraw::DrawViewDimension] Dimension043
  AngleOverride = false
  Arbitrary = false
  ArbitraryTolerances = false
  EqualTolerance = true
  ExtensionAngle = 0
  FormatSpec = ⌀%.2f
  FormatSpecOverTolerance = %+.2f
  FormatSpecUnderTolerance = %+.2f
  Inverted = false
  LineAngle = 0
  LockPosition = false
  MeasureType = 1
  OverTolerance = 0
  References2D = -> [ProjItem004]
  Rotation = 0
  ScaleType = 0
  TheoreticalExact = false
  Type = 5
  UnderTolerance = 0
  X = 28.5428
  Y = 24.4408
FEATURE [TechDraw::DrawViewDimension] Dimension044
  AngleOverride = false
  Arbitrary = false
  ArbitraryTolerances = false
  EqualTolerance = true
  ExtensionAngle = 0
  FormatSpec = ⌀%.2f
  FormatSpecOverTolerance = %+.2f
  FormatSpecUnderTolerance = %+.2f
  Inverted = false
  LineAngle = 0
  LockPosition = false
  MeasureType = 1
  OverTolerance = 0
  References2D = -> [ProjItem007]
  Rotation = 0
  ScaleType = 0
  TheoreticalExact = false
  Type = 5
  UnderTolerance = 0
  X = 31.961
  Y = 34.1829
FEATURE [TechDraw::DrawViewDimension] Dimension045
  AngleOverride = false
  Arbitrary = false
  ArbitraryTolerances = false
  EqualTolerance = true
  ExtensionAngle = 0
  FormatSpec = %.2f
  FormatSpecOverTolerance = %+.2f
  FormatSpecUnderTolerance = %+.2f
  Inverted = false
  LineAngle = 0
  LockPosition = false
  MeasureType = 1
  OverTolerance = 0
  References2D = -> [ProjItem007]
  Rotation = 0
  ScaleType = 0
  TheoreticalExact = false
  Type = 2
  UnderTolerance = 0
  X = -30.8186
  Y = 3.1964
FEATURE [TechDraw::DrawViewDimension] Dimension046
  AngleOverride = false
  Arbitrary = false
  ArbitraryTolerances = false
  EqualTolerance = true
  ExtensionAngle = 0
  FormatSpec = %.2f
  FormatSpecOverTolerance = %+.2f
  FormatSpecUnderTolerance = %+.2f
  Inverted = false
  LineAngle = 0
  LockPosition = false
  MeasureType = 1
  OverTolerance = 0
  References2D = -> [ProjItem006]
  Rotation = 0
  ScaleType = 0
  TheoreticalExact = false
  Type = 1
  UnderTolerance = 0
  X = -0.545356
  Y = 32.9142
FEATURE [TechDraw::DrawViewAnnotation] Annotation  label="FrontAnnotation"
  Font = Lucida Grande
  LineSpace = 80
  LockPosition = false
  MaxWidth = -1
  Rotation = 0
  ScaleType = 0
  Text = Front
  TextSize = 5
  TextStyle = 0
  X = 142
  Y = 137.5
FEATURE [TechDraw::DrawViewAnnotation] Annotation001  label="RightAnnotation"
  Font = Lucida Grande
  LineSpace = 80
  LockPosition = false
  MaxWidth = -1
  Rotation = 0
  ScaleType = 0
  Text = Right
  TextSize = 5
  TextStyle = 0
  X = 74
  Y = 137.5
FEATURE [TechDraw::DrawViewAnnotation] Annotation002  label="TopAnnotation"
  Font = Lucida Grande
  LineSpace = 80
  LockPosition = false
  MaxWidth = -1
  Rotation = 0
  ScaleType = 0
  Text = Top
  TextSize = 5
  TextStyle = 0
  X = 141
  Y = 59.5
FEATURE [TechDraw::DrawViewDimension] Dimension047
  AngleOverride = false
  Arbitrary = false
  ArbitraryTolerances = false
  EqualTolerance = true
  ExtensionAngle = 0
  FormatSpec = %.2f
  FormatSpecOverTolerance = %+.2f
  FormatSpecUnderTolerance = %+.2f
  Inverted = false
  LineAngle = 0
  LockPosition = false
  MeasureType = 1
  OverTolerance = 0
  References2D = -> [ProjItem004]
  Rotation = 0
  ScaleType = 0
  TheoreticalExact = false
  Type = 2
  UnderTolerance = 0
  X = 21.9855
  Y = 4.625
FEATURE [TechDraw::DrawPage] Page004  label="BracketDrawings"
  KeepUpdated = true
  NextBalloonIndex = 1
  ProjectionType = 0
  Template = -> Template004
  Views = -> [ProjGroup004,Dimension033,Dimension034,Dimension035,Dimension036,Dimension037,Dimension038,Dimension039,Dimension040,Dimension041,Dimension042,Dimension043,Dimension044,Dimension045,Dimension046,Annotation,Annotation001,Annotation002,Dimension047]
FEATURE [TechDraw::DrawSVGTemplate] Template005
  Height = 297
  Orientation = 0
  Width = 210
FEATURE [TechDraw::DrawSVGTemplate] Template006
  Height = 297
  Orientation = 0
  Width = 210
FEATURE [Sketcher::SketchObject] Sketch008  label="AngledSensorHoles"
  AttachmentOffset = pos=(0,0,3) rot=(0,0,1;0rad)
  ExternalGeometry = -> [Sketch005]
  FullyConstrained = true
  MapMode = 5
  Placement = pos=(0,0,3) rot=(0,0,1;0rad)
  Support = -> [XY_Plane]
  sketch-geometry (6):
    g0: LineSegment StartX=-44 StartY=-75 StartZ=0 EndX=-30 EndY=-75 EndZ=0
    g1: LineSegment StartX=30 StartY=-75 StartZ=0 EndX=44 EndY=-75 EndZ=0
    g2: Circle CenterX=-44 CenterY=-89 CenterZ=0 NormalX=0 NormalY=0 NormalZ=1 AngleXU=0 Radius=1
    g3: Circle CenterX=44 CenterY=-89 CenterZ=0 NormalX=0 NormalY=0 NormalZ=1 AngleXU=0 Radius=1
    g4: LineSegment StartX=-44 StartY=-75 StartZ=0 EndX=-44 EndY=-89 EndZ=0
    g5: LineSegment StartX=44 StartY=-75 StartZ=0 EndX=44 EndY=-89 EndZ=0
  constraints (14):
    c: Coincident(g0,g-3)
    c: Coincident(g0,g-4)
    c: Coincident(g1,g-6)
    c: Coincident(g1,g-5)
    c: Coincident(g4,g0)
    c: Coincident(g4,g2)
    c: Coincident(g5,g1)
    c: Coincident(g5,g3)
    c: Equal(g3,g-5)
    c: Equal(g2,g-3)
    c: Equal(g4,g0)
    c: Equal(g5,g1)
    c: Perpendicular(g0,g4)
    c: Perpendicular(g1,g5)
FEATURE [PartDesign::ShapeBinder] ShapeBinder016
  Support = -> [Sketch008]
  TraceSupport = false
FEATURE [PartDesign::Pocket] Pocket011
  BaseFeature = -> Pocket010
  Direction = (0,0,-1)
  Length = 5
  Length2 = 5
  Profile = -> ShapeBinder016
  Type = 1
FEATURE [PartDesign::Body] Body001  label="ChassisPlate"
  Group = -> [ShapeBinder,Pad,ShapeBinder001,Pocket,ShapeBinder006,Pocket001,ShapeBinder007,Pocket002,ShapeBinder009,Pocket003,ShapeBinder010,Pocket004,ShapeBinder011,Pocket005,Binder003,Pocket008,Binder004,Pocket009,Binder005,Pocket010,ShapeBinder016,Pocket011]
  Origin = -> Origin001
  Tip = -> Pocket011
FEATURE [TechDraw::DrawProjGroupItem] ProjItem  label="Front"
  CoarseView = false
  Direction = (0,0,1)
  Focus = 100
  HardHidden = false
  IsoCount = 0
  IsoHidden = false
  IsoVisible = false
  LockPosition = true
  Perspective = false
  Rotation = 0
  RotationVector = (1,0,0)
  ScaleType = 2
  SeamHidden = false
  SeamVisible = true
  SmoothHidden = false
  SmoothVisible = true
  Source = -> [Body001]
  Type = 0
  X = 0
  XDirection = (-1,-1e-16,0)
  Y = 0
FEATURE [TechDraw::DrawProjGroup] ProjGroup
  Anchor = -> ProjItem
  AutoDistribute = true
  LockPosition = false
  ProjectionType = 0
  Rotation = 0
  ScaleType = 0
  Source = -> [Body001]
  Views = -> [ProjItem]
  X = 105
  Y = 148.5
  spacingX = 15
  spacingY = 15
FEATURE [TechDraw::DrawViewDimension] Dimension
  AngleOverride = false
  Arbitrary = false
  ArbitraryTolerances = false
  EqualTolerance = true
  ExtensionAngle = 0
  FormatSpec = ⌀%.2f
  FormatSpecOverTolerance = %+.2f
  FormatSpecUnderTolerance = %+.2f
  Inverted = false
  LineAngle = 0
  LockPosition = false
  MeasureType = 1
  OverTolerance = 0
  References2D = -> [ProjItem]
  Rotation = 0
  ScaleType = 0
  TheoreticalExact = false
  Type = 5
  UnderTolerance = 0
  X = 50.1529
  Y = 70.5531
FEATURE [TechDraw::DrawViewDimension] Dimension002
  AngleOverride = false
  Arbitrary = false
  ArbitraryTolerances = false
  EqualTolerance = true
  ExtensionAngle = 0
  FormatSpec = %.2f
  FormatSpecOverTolerance = %+.2f
  FormatSpecUnderTolerance = %+.2f
  Inverted = false
  LineAngle = 0
  LockPosition = false
  MeasureType = 1
  OverTolerance = 0
  References2D = -> [ProjItem]
  Rotation = 0
  ScaleType = 0
  TheoreticalExact = false
  Type = 1
  UnderTolerance = 0
  X = 2.04208
  Y = 121.051
FEATURE [TechDraw::DrawViewDimension] Dimension004
  AngleOverride = false
  Arbitrary = false
  ArbitraryTolerances = false
  EqualTolerance = true
  ExtensionAngle = 0
  FormatSpec = %.2f
  FormatSpecOverTolerance = %+.2f
  FormatSpecUnderTolerance = %+.2f
  Inverted = false
  LineAngle = 0
  LockPosition = false
  MeasureType = 1
  OverTolerance = 0
  References2D = -> [ProjItem]
  Rotation = 0
  ScaleType = 0
  TheoreticalExact = false
  Type = 1
  UnderTolerance = 0
  X = 1.29717
  Y = 110.802
FEATURE [TechDraw::DrawViewDimension] Dimension005
  AngleOverride = false
  Arbitrary = false
  ArbitraryTolerances = false
  EqualTolerance = true
  ExtensionAngle = 0
  FormatSpec = %.2f
  FormatSpecOverTolerance = %+.2f
  FormatSpecUnderTolerance = %+.2f
  Inverted = false
  LineAngle = 0
  LockPosition = false
  MeasureType = 1
  OverTolerance = 0
  References2D = -> [ProjItem]
  Rotation = 0
  ScaleType = 0
  TheoreticalExact = false
  Type = 2
  UnderTolerance = 0
  X = 83.6298
  Y = 95.1317
FEATURE [TechDraw::DrawViewDimension] Dimension006
  AngleOverride = false
  Arbitrary = false
  ArbitraryTolerances = false
  EqualTolerance = true
  ExtensionAngle = 0
  FormatSpec = %.2f
  FormatSpecOverTolerance = %+.2f
  FormatSpecUnderTolerance = %+.2f
  Inverted = false
  LineAngle = 0
  LockPosition = false
  MeasureType = 1
  OverTolerance = 0
  References2D = -> [ProjItem]
  Rotation = 0
  ScaleType = 0
  TheoreticalExact = false
  Type = 2
  UnderTolerance = 0
  X = 86.1661
  Y = 1.23328
FEATURE [TechDraw::DrawViewDimension] Dimension007
  AngleOverride = false
  Arbitrary = false
  ArbitraryTolerances = false
  EqualTolerance = true
  ExtensionAngle = 0
  FormatSpec = %.2f
  FormatSpecOverTolerance = %+.2f
  FormatSpecUnderTolerance = %+.2f
  Inverted = false
  LineAngle = 0
  LockPosition = false
  MeasureType = 1
  OverTolerance = 0
  References2D = -> [ProjItem]
  Rotation = 0
  ScaleType = 0
  TheoreticalExact = false
  Type = 2
  UnderTolerance = 0
  X = 28.9009
  Y = -87.2406
FEATURE [TechDraw::DrawViewDimension] Dimension008
  AngleOverride = false
  Arbitrary = false
  ArbitraryTolerances = false
  EqualTolerance = true
  ExtensionAngle = 0
  FormatSpec = %.2f
  FormatSpecOverTolerance = %+.2f
  FormatSpecUnderTolerance = %+.2f
  Inverted = false
  LineAngle = 0
  LockPosition = false
  MeasureType = 1
  OverTolerance = 0
  References2D = -> [ProjItem]
  Rotation = 0
  ScaleType = 0
  TheoreticalExact = false
  Type = 1
  UnderTolerance = 0
  X = 0.423435
  Y = -60.3088
FEATURE [TechDraw::DrawViewDimension] Dimension009
  AngleOverride = false
  Arbitrary = false
  ArbitraryTolerances = false
  EqualTolerance = true
  ExtensionAngle = 0
  FormatSpec = %.2f
  FormatSpecOverTolerance = %+.2f
  FormatSpecUnderTolerance = %+.2f
  Inverted = false
  LineAngle = 0
  LockPosition = false
  MeasureType = 1
  OverTolerance = 0
  References2D = -> [ProjItem]
  Rotation = 0
  ScaleType = 0
  TheoreticalExact = false
  Type = 1
  UnderTolerance = 0
  X = -69
  Y = 72.7358
FEATURE [TechDraw::DrawViewDimension] Dimension010
  AngleOverride = false
  Arbitrary = false
  ArbitraryTolerances = false
  EqualTolerance = true
  ExtensionAngle = 0
  FormatSpec = %.2f
  FormatSpecOverTolerance = %+.2f
  FormatSpecUnderTolerance = %+.2f
  Inverted = false
  LineAngle = 0
  LockPosition = false
  MeasureType = 1
  OverTolerance = 0
  References2D = -> [ProjItem]
  Rotation = 0
  ScaleType = 0
  TheoreticalExact = false
  Type = 2
  UnderTolerance = 0
  X = -52.7358
  Y = 53.9906
FEATURE [TechDraw::DrawViewDimension] Dimension011
  AngleOverride = false
  Arbitrary = false
  ArbitraryTolerances = false
  EqualTolerance = true
  ExtensionAngle = 0
  FormatSpec = %.2f
  FormatSpecOverTolerance = %+.2f
  FormatSpecUnderTolerance = %+.2f
  Inverted = false
  LineAngle = 0
  LockPosition = false
  MeasureType = 1
  OverTolerance = 0
  References2D = -> [ProjItem]
  Rotation = 0
  ScaleType = 0
  TheoreticalExact = false
  Type = 2
  UnderTolerance = 0
  X = -53.1368
  Y = 83.3939
FEATURE [TechDraw::DrawViewDimension] Dimension014
  AngleOverride = false
  Arbitrary = false
  ArbitraryTolerances = false
  EqualTolerance = true
  ExtensionAngle = 0
  FormatSpec = ⌀%.2f
  FormatSpecOverTolerance = %+.2f
  FormatSpecUnderTolerance = %+.2f
  Inverted = false
  LineAngle = 0
  LockPosition = false
  MeasureType = 1
  OverTolerance = 0
  References2D = -> [ProjItem]
  Rotation = 0
  ScaleType = 0
  TheoreticalExact = false
  Type = 5
  UnderTolerance = 0
  X = 30.6276
  Y = -55.1297
FEATURE [TechDraw::DrawViewDimension] Dimension022
  AngleOverride = false
  Arbitrary = false
  ArbitraryTolerances = false
  EqualTolerance = true
  ExtensionAngle = 0
  FormatSpec = %.2f
  FormatSpecOverTolerance = %+.2f
  FormatSpecUnderTolerance = %+.2f
  Inverted = false
  LineAngle = 0
  LockPosition = false
  MeasureType = 1
  OverTolerance = 0
  References2D = -> [ProjItem]
  Rotation = 0
  ScaleType = 0
  TheoreticalExact = false
  Type = 1
  UnderTolerance = 0
  X = -50.6554
  Y = 111.263
FEATURE [TechDraw::DrawViewDimension] Dimension023
  AngleOverride = false
  Arbitrary = false
  ArbitraryTolerances = false
  EqualTolerance = true
  ExtensionAngle = 0
  FormatSpec = %.2f
  FormatSpecOverTolerance = %+.2f
  FormatSpecUnderTolerance = %+.2f
  Inverted = false
  LineAngle = 0
  LockPosition = false
  MeasureType = 1
  OverTolerance = 0
  References2D = -> [ProjItem]
  Rotation = 0
  ScaleType = 0
  TheoreticalExact = false
  Type = 1
  UnderTolerance = 0
  X = 50
  Y = 110.28
FEATURE [TechDraw::DrawViewDimension] Dimension024
  AngleOverride = false
  Arbitrary = false
  ArbitraryTolerances = false
  EqualTolerance = true
  ExtensionAngle = 0
  FormatSpec = %.2f
  FormatSpecOverTolerance = %+.2f
  FormatSpecUnderTolerance = %+.2f
  Inverted = false
  LineAngle = 0
  LockPosition = false
  MeasureType = 1
  OverTolerance = 0
  References2D = -> [ProjItem]
  Rotation = 0
  ScaleType = 0
  TheoreticalExact = false
  Type = 1
  UnderTolerance = 0
  X = -41.0473
  Y = -60.1593
FEATURE [TechDraw::DrawPage] Page  label="CuttingDimensions"
  KeepUpdated = true
  NextBalloonIndex = 1
  ProjectionType = 0
  Template = -> Template
  Views = -> [ProjGroup,Dimension,Dimension002,Dimension004,Dimension005,Dimension006,Dimension007,Dimension008,Dimension009,Dimension010,Dimension011,Dimension014,Dimension022,Dimension023,Dimension024]
FEATURE [TechDraw::DrawProjGroupItem] ProjItem002  label="Front002"
  CoarseView = false
  Direction = (0,0,1)
  Focus = 100
  HardHidden = false
  IsoCount = 0
  IsoHidden = false
  IsoVisible = false
  LockPosition = true
  Perspective = false
  Rotation = 0
  RotationVector = (-1,0,0)
  ScaleType = 2
  SeamHidden = false
  SeamVisible = true
  SmoothHidden = false
  SmoothVisible = true
  Source = -> [Body001]
  Type = 0
  X = 0
  XDirection = (-1,0,0)
  Y = 0
FEATURE [TechDraw::DrawProjGroup] ProjGroup002
  Anchor = -> ProjItem002
  AutoDistribute = true
  LockPosition = false
  ProjectionType = 0
  Rotation = 0
  ScaleType = 0
  Source = -> [Body001]
  Views = -> [ProjItem002]
  X = 105
  Y = 148.5
  spacingX = 15
  spacingY = 15
FEATURE [TechDraw::DrawViewDimension] Dimension026
  AngleOverride = false
  Arbitrary = false
  ArbitraryTolerances = false
  EqualTolerance = true
  ExtensionAngle = 0
  FormatSpec = ⌀%.2f
  FormatSpecOverTolerance = %+.2f
  FormatSpecUnderTolerance = %+.2f
  Inverted = false
  LineAngle = 0
  LockPosition = false
  MeasureType = 1
  OverTolerance = 0
  References2D = -> [ProjItem002]
  Rotation = 0
  ScaleType = 0
  TheoreticalExact = false
  Type = 5
  UnderTolerance = 0
  X = 38.1284
  Y = 75.0527
FEATURE [TechDraw::DrawViewDimension] Dimension027
  AngleOverride = false
  Arbitrary = false
  ArbitraryTolerances = false
  EqualTolerance = true
  ExtensionAngle = 0
  FormatSpec = ⌀%.2f
  FormatSpecOverTolerance = %+.2f
  FormatSpecUnderTolerance = %+.2f
  Inverted = false
  LineAngle = 0
  LockPosition = false
  MeasureType = 1
  OverTolerance = 0
  References2D = -> [ProjItem002]
  Rotation = 0
  ScaleType = 0
  TheoreticalExact = false
  Type = 5
  UnderTolerance = 0
  X = -12.5
  Y = 69.0146
FEATURE [TechDraw::DrawViewDimension] Dimension048
  AngleOverride = false
  Arbitrary = false
  ArbitraryTolerances = false
  EqualTolerance = true
  ExtensionAngle = 0
  FormatSpec = %.2f
  FormatSpecOverTolerance = %+.2f
  FormatSpecUnderTolerance = %+.2f
  Inverted = false
  LineAngle = 0
  LockPosition = false
  MeasureType = 1
  OverTolerance = 0
  References2D = -> [ProjItem002]
  Rotation = 0
  ScaleType = 0
  TheoreticalExact = false
  Type = 2
  UnderTolerance = 0
  X = -82.4306
  Y = -95.3056
FEATURE [TechDraw::DrawViewDimension] Dimension049
  AngleOverride = false
  Arbitrary = false
  ArbitraryTolerances = false
  EqualTolerance = true
  ExtensionAngle = 0
  FormatSpec = %.2f
  FormatSpecOverTolerance = %+.2f
  FormatSpecUnderTolerance = %+.2f
  Inverted = false
  LineAngle = 0
  LockPosition = false
  MeasureType = 1
  OverTolerance = 0
  References2D = -> [ProjItem002]
  Rotation = 0
  ScaleType = 0
  TheoreticalExact = false
  Type = 1
  UnderTolerance = 0
  X = -73
  Y = -106.819
FEATURE [TechDraw::DrawViewDimension] Dimension050
  AngleOverride = false
  Arbitrary = false
  ArbitraryTolerances = false
  EqualTolerance = true
  ExtensionAngle = 0
  FormatSpec = ⌀%.2f
  FormatSpecOverTolerance = %+.2f
  FormatSpecUnderTolerance = %+.2f
  Inverted = false
  LineAngle = 0
  LockPosition = false
  MeasureType = 1
  OverTolerance = 0
  References2D = -> [ProjItem002]
  Rotation = 0
  ScaleType = 0
  TheoreticalExact = false
  Type = 5
  UnderTolerance = 0
  X = -40.625
  Y = -73.2639
FEATURE [TechDraw::DrawViewDimension] Dimension051
  AngleOverride = false
  Arbitrary = false
  ArbitraryTolerances = false
  EqualTolerance = true
  ExtensionAngle = 0
  FormatSpec = %.2f
  FormatSpecOverTolerance = %+.2f
  FormatSpecUnderTolerance = %+.2f
  Inverted = false
  LineAngle = 0
  LockPosition = false
  MeasureType = 1
  OverTolerance = 0
  References2D = -> [ProjItem002]
  Rotation = 0
  ScaleType = 0
  TheoreticalExact = false
  Type = 2
  UnderTolerance = 0
  X = -17.6667
  Y = 89.1528
FEATURE [TechDraw::DrawViewDimension] Dimension052
  AngleOverride = false
  Arbitrary = false
  ArbitraryTolerances = false
  EqualTolerance = true
  ExtensionAngle = 0
  FormatSpec = %.2f
  FormatSpecOverTolerance = %+.2f
  FormatSpecUnderTolerance = %+.2f
  Inverted = false
  LineAngle = 0
  LockPosition = false
  MeasureType = 1
  OverTolerance = 0
  References2D = -> [ProjItem002]
  Rotation = 0
  ScaleType = 0
  TheoreticalExact = false
  Type = 2
  UnderTolerance = 0
  X = -67.5
  Y = -73
FEATURE [TechDraw::DrawViewDimension] Dimension053
  AngleOverride = false
  Arbitrary = false
  ArbitraryTolerances = false
  EqualTolerance = true
  ExtensionAngle = 0
  FormatSpec = %.2f
  FormatSpecOverTolerance = %+.2f
  FormatSpecUnderTolerance = %+.2f
  Inverted = false
  LineAngle = 0
  LockPosition = false
  MeasureType = 1
  OverTolerance = 0
  References2D = -> [ProjItem002]
  Rotation = 0
  ScaleType = 0
  TheoreticalExact = false
  Type = 1
  UnderTolerance = 0
  X = -59.8472
  Y = 70.2778
FEATURE [TechDraw::DrawViewDimension] Dimension054
  AngleOverride = false
  Arbitrary = false
  ArbitraryTolerances = false
  EqualTolerance = true
  ExtensionAngle = 0
  FormatSpec = %.2f
  FormatSpecOverTolerance = %+.2f
  FormatSpecUnderTolerance = %+.2f
  Inverted = false
  LineAngle = 0
  LockPosition = false
  MeasureType = 1
  OverTolerance = 0
  References2D = -> [ProjItem002]
  Rotation = 0
  ScaleType = 0
  TheoreticalExact = false
  Type = 1
  UnderTolerance = 0
  X = -37.3472
  Y = 69.9306
FEATURE [TechDraw::DrawPage] Page002  label="ChassisBevelTemplate"
  KeepUpdated = true
  NextBalloonIndex = 1
  ProjectionType = 0
  Template = -> Template002
  Views = -> [ProjGroup002,Dimension026,Dimension027,Dimension048,Dimension049,Dimension050,Dimension051,Dimension052,Dimension053,Dimension054]
FEATURE [TechDraw::DrawProjGroupItem] ProjItem009  label="Front006"
  CoarseView = false
  Direction = (0,0,1)
  Focus = 100
  HardHidden = false
  IsoCount = 0
  IsoHidden = false
  IsoVisible = false
  LockPosition = true
  Perspective = false
  Rotation = 0
  RotationVector = (1,0,0)
  ScaleType = 2
  SeamHidden = false
  SeamVisible = true
  SmoothHidden = false
  SmoothVisible = true
  Source = -> [Body001]
  Type = 0
  X = 0
  XDirection = (1,0,0)
  Y = 0
FEATURE [TechDraw::DrawProjGroup] ProjGroup006
  Anchor = -> ProjItem009
  AutoDistribute = true
  LockPosition = false
  ProjectionType = 0
  Rotation = 0
  ScaleType = 0
  Source = -> [Body001]
  Views = -> [ProjItem009]
  X = 105
  Y = 148.5
  spacingX = 15
  spacingY = 15
FEATURE [TechDraw::DrawViewDimension] Dimension066
  AngleOverride = false
  Arbitrary = false
  ArbitraryTolerances = false
  EqualTolerance = true
  ExtensionAngle = 0
  FormatSpec = %.2f
  FormatSpecOverTolerance = %+.2f
  FormatSpecUnderTolerance = %+.2f
  Inverted = false
  LineAngle = 0
  LockPosition = false
  MeasureType = 1
  OverTolerance = 0
  References2D = -> [ProjItem009]
  Rotation = 0
  ScaleType = 0
  TheoreticalExact = false
  Type = 2
  UnderTolerance = 0
  X = -83.2519
  Y = -29.7281
FEATURE [TechDraw::DrawViewDimension] Dimension067
  AngleOverride = false
  Arbitrary = false
  ArbitraryTolerances = false
  EqualTolerance = true
  ExtensionAngle = 0
  FormatSpec = ⌀%.2f
  FormatSpecOverTolerance = %+.2f
  FormatSpecUnderTolerance = %+.2f
  Inverted = false
  LineAngle = 0
  LockPosition = false
  MeasureType = 1
  OverTolerance = 0
  References2D = -> [ProjItem009]
  Rotation = 0
  ScaleType = 0
  TheoreticalExact = false
  Type = 5
  UnderTolerance = 0
  X = -28.5152
  Y = -82.3052
FEATURE [TechDraw::DrawViewDimension] Dimension068
  AngleOverride = false
  Arbitrary = false
  ArbitraryTolerances = false
  EqualTolerance = true
  ExtensionAngle = 0
  FormatSpec = ⌀%.2f
  FormatSpecOverTolerance = %+.2f
  FormatSpecUnderTolerance = %+.2f
  Inverted = false
  LineAngle = 0
  LockPosition = false
  MeasureType = 1
  OverTolerance = 0
  References2D = -> [ProjItem009]
  Rotation = 0
  ScaleType = 0
  TheoreticalExact = false
  Type = 5
  UnderTolerance = 0
  X = -45.6081
  Y = -17.1739
FEATURE [TechDraw::DrawViewDimension] Dimension069
  AngleOverride = false
  Arbitrary = false
  ArbitraryTolerances = false
  EqualTolerance = true
  ExtensionAngle = 0
  FormatSpec = %.2f
  FormatSpecOverTolerance = %+.2f
  FormatSpecUnderTolerance = %+.2f
  Inverted = false
  LineAngle = 0
  LockPosition = false
  MeasureType = 1
  OverTolerance = 0
  References2D = -> [ProjItem009]
  Rotation = 0
  ScaleType = 0
  TheoreticalExact = false
  Type = 2
  UnderTolerance = 0
  X = -57.9309
  Y = -80.243
FEATURE [TechDraw::DrawPage] Page006  label="ChassisPlateWallFollowHoles"
  KeepUpdated = true
  NextBalloonIndex = 1
  ProjectionType = 0
  Template = -> Template006
  Views = -> [ProjGroup006,Dimension066,Dimension067,Dimension068,Dimension069]
FEATURE [Sketcher::SketchObject] Sketch009  label="BNO055"
  AttachmentOffset = pos=(0,0,33) rot=(0,0,1;0rad)
  ExternalGeometry = -> [Sketch004]
  FullyConstrained = true
  MapMode = 5
  Placement = pos=(0,0,33) rot=(0,0,1;0rad)
  Support = -> [XY_Plane]
  sketch-geometry (14):
    g0: ArcOfCircle CenterX=-45 CenterY=80.24 CenterZ=0 NormalX=0 NormalY=0 NormalZ=1 AngleXU=0 Radius=2.54 StartAngle=1.5708 EndAngle=3.14159
    g1: LineSegment StartX=-45 StartY=82.78 StartZ=0 EndX=-23.41 EndY=82.78 EndZ=0
    g2: ArcOfCircle CenterX=-23.41 CenterY=80.24 CenterZ=0 NormalX=0 NormalY=0 NormalZ=1 AngleXU=0 Radius=2.54 StartAngle=2.7e-15 EndAngle=1.5708
    g3: LineSegment StartX=-20.87 StartY=80.24 StartZ=0 EndX=-20.87 EndY=65 EndZ=0
    g4: ArcOfCircle CenterX=-23.41 CenterY=65 CenterZ=0 NormalX=0 NormalY=0 NormalZ=1 AngleXU=0 Radius=2.54 StartAngle=4.71239 EndAngle=6.28319
    g5: LineSegment StartX=-23.41 StartY=62.46 StartZ=0 EndX=-45 EndY=62.46 EndZ=0
    g6: ArcOfCircle CenterX=-45 CenterY=65 CenterZ=0 NormalX=0 NormalY=0 NormalZ=1 AngleXU=0 Radius=2.54 StartAngle=3.14159 EndAngle=4.71239
    g7: LineSegment StartX=-47.54 StartY=65 StartZ=0 EndX=-47.54 EndY=80.24 EndZ=0
    g8: GeomPoint X=-47.54 Y=82.78 Z=0
    g9: GeomPoint X=-20.87 Y=62.46 Z=0
    g10: Circle CenterX=-45 CenterY=80.24 CenterZ=0 NormalX=0 NormalY=0 NormalZ=1 AngleXU=0 Radius=1.27
    g11: Circle CenterX=-23.41 CenterY=80.24 CenterZ=0 NormalX=0 NormalY=0 NormalZ=1 AngleXU=0 Radius=1.27
    g12: Circle CenterX=-23.41 CenterY=65 CenterZ=0 NormalX=0 NormalY=0 NormalZ=1 AngleXU=0 Radius=1.27
    g13: Circle CenterX=-45 CenterY=65 CenterZ=0 NormalX=0 NormalY=0 NormalZ=1 AngleXU=0 Radius=1.27
  constraints (32):
    c: Tangent(g0,g1) = 1.5708
    c: Tangent(g1,g2) = 1.5708
    c: Tangent(g2,g3) = 1.5708
    c: Tangent(g3,g4) = 1.5708
    c: Tangent(g4,g5) = 1.5708
    c: Tangent(g5,g6) = 1.5708
    c: Tangent(g6,g7) = 1.5708
    c: Tangent(g7,g0) = 1.5708
    c: Horizontal(g1)
    c: Horizontal(g5)
    c: Vertical(g3)
    c: Equal(g0,g2)
    c: Equal(g2,g4)
    c: Equal(g4,g6)
    c: PointOnObject(g8,g1)
    c: PointOnObject(g8,g7)
    c: PointOnObject(g9,g3)
    c: PointOnObject(g9,g5)
    c: DistanceX(g0,g2) = 26.67
    c: DistanceY(g5,g0) = 20.32
    c: Coincident(g10,g0)
    c: Coincident(g11,g2)
    c: Coincident(g12,g4)
    c: Coincident(g13,g6)
    c: Equal(g10,g13)
    c: Equal(g13,g12)
    c: Equal(g12,g11)
    c: Diameter(g10) = 2.54
    c: DistanceX(g-4,g6) = 30
    c: DistanceY(g-4,g6) = 15
    c: DistanceY(g6,g0) = 15.24
    c: Vertical(g7)
FEATURE [PartDesign::Body] Body  label="SketchMain"
  Group = -> [Sketch,Sketch001,Sketch002,Sketch003,Sketch004,Sketch005,Sketch007,Sketch008,Sketch009]
  Origin = -> Origin
FEATURE [PartDesign::ShapeBinder] ShapeBinder017
  Support = -> [Sketch009]
  TraceSupport = false
FEATURE [PartDesign::Pocket] Pocket012
  BaseFeature = -> Pad006
  Direction = (0,0,-1)
  Length = 5
  Length2 = 5
  Profile = -> ShapeBinder017
  Type = 1
FEATURE [PartDesign::Body] Body007  label="DaughterCard"
  Group = -> [ShapeBinder012,Pad006,ShapeBinder017,Pocket012]
  Origin = -> Origin007
  Tip = -> Pocket012
FEATURE [TechDraw::DrawProjGroupItem] ProjItem003  label="Front003"
  CoarseView = false
  Direction = (0,0,1)
  Focus = 100
  HardHidden = false
  IsoCount = 0
  IsoHidden = false
  IsoVisible = false
  LockPosition = true
  Perspective = false
  Rotation = 0
  RotationVector = (1,0,0)
  ScaleType = 2
  SeamHidden = false
  SeamVisible = true
  SmoothHidden = false
  SmoothVisible = true
  Source = -> [Body007]
  Type = 0
  X = 0
  XDirection = (1,0,0)
  Y = 0
FEATURE [TechDraw::DrawProjGroup] ProjGroup003
  Anchor = -> ProjItem003
  AutoDistribute = true
  LockPosition = false
  ProjectionType = 0
  Rotation = 0
  ScaleType = 0
  Source = -> [Body007]
  Views = -> [ProjItem003]
  X = 104.394
  Y = 152.44
  spacingX = 15
  spacingY = 15
FEATURE [TechDraw::DrawProjGroupItem] ProjItem008  label="Front005"
  CoarseView = false
  Direction = (0,0,1)
  Focus = 100
  HardHidden = false
  IsoCount = 0
  IsoHidden = false
  IsoVisible = false
  LockPosition = true
  Perspective = false
  Rotation = 0
  RotationVector = (1,0,0)
  ScaleType = 2
  SeamHidden = false
  SeamVisible = true
  SmoothHidden = false
  SmoothVisible = true
  Source = -> [Body001,Body007,Body008,Body009]
  Type = 0
  X = 0
  XDirection = (1,0,0)
  Y = 0
FEATURE [TechDraw::DrawProjGroup] ProjGroup005
  Anchor = -> ProjItem008
  AutoDistribute = true
  LockPosition = false
  ProjectionType = 0
  Rotation = 0
  ScaleType = 0
  Source = -> [Body001,Body007,Body008,Body009]
  Views = -> [ProjItem008]
  X = 105
  Y = 148.5
  spacingX = 15
  spacingY = 15
FEATURE [TechDraw::DrawViewDimension] Dimension055
  AngleOverride = false
  Arbitrary = false
  ArbitraryTolerances = false
  EqualTolerance = true
  ExtensionAngle = 0
  FormatSpec = %.2f
  FormatSpecOverTolerance = %+.2f
  FormatSpecUnderTolerance = %+.2f
  Inverted = false
  LineAngle = 0
  LockPosition = false
  MeasureType = 1
  OverTolerance = 0
  References2D = -> [ProjItem008]
  Rotation = 0
  ScaleType = 0
  TheoreticalExact = false
  Type = 2
  UnderTolerance = 0
  X = -11.8456
  Y = -84.3766
FEATURE [TechDraw::DrawViewDimension] Dimension056
  AngleOverride = false
  Arbitrary = false
  ArbitraryTolerances = false
  EqualTolerance = true
  ExtensionAngle = 0
  FormatSpec = %.2f
  FormatSpecOverTolerance = %+.2f
  FormatSpecUnderTolerance = %+.2f
  Inverted = false
  LineAngle = 0
  LockPosition = false
  MeasureType = 1
  OverTolerance = 0
  References2D = -> [ProjItem008]
  Rotation = 0
  ScaleType = 0
  TheoreticalExact = false
  Type = 1
  UnderTolerance = 0
  X = -59.2753
  Y = -64.1585
FEATURE [TechDraw::DrawViewDimension] Dimension057
  AngleOverride = false
  Arbitrary = false
  ArbitraryTolerances = false
  EqualTolerance = true
  ExtensionAngle = 0
  FormatSpec = %.2f
  FormatSpecOverTolerance = %+.2f
  FormatSpecUnderTolerance = %+.2f
  Inverted = false
  LineAngle = 0
  LockPosition = false
  MeasureType = 1
  OverTolerance = 0
  References2D = -> [ProjItem008]
  Rotation = 0
  ScaleType = 0
  TheoreticalExact = false
  Type = 1
  UnderTolerance = 0
  X = -36.7753
  Y = -64.3832
FEATURE [TechDraw::DrawViewDimension] Dimension058
  AngleOverride = false
  Arbitrary = false
  ArbitraryTolerances = false
  EqualTolerance = true
  ExtensionAngle = 0
  FormatSpec = %.2f
  FormatSpecOverTolerance = %+.2f
  FormatSpecUnderTolerance = %+.2f
  Inverted = false
  LineAngle = 0
  LockPosition = false
  MeasureType = 1
  OverTolerance = 0
  References2D = -> [ProjItem008]
  Rotation = 0
  ScaleType = 0
  TheoreticalExact = false
  Type = 1
  UnderTolerance = 0
  X = -73.4493
  Y = 68.7116
FEATURE [TechDraw::DrawViewDimension] Dimension059
  AngleOverride = false
  Arbitrary = false
  ArbitraryTolerances = false
  EqualTolerance = true
  ExtensionAngle = 0
  FormatSpec = %.2f
  FormatSpecOverTolerance = %+.2f
  FormatSpecUnderTolerance = %+.2f
  Inverted = false
  LineAngle = 0
  LockPosition = false
  MeasureType = 1
  OverTolerance = 0
  References2D = -> [ProjItem008]
  Rotation = 0
  ScaleType = 0
  TheoreticalExact = false
  Type = 2
  UnderTolerance = 0
  X = -67.5
  Y = 77
FEATURE [TechDraw::DrawViewDimension] Dimension060
  AngleOverride = false
  Arbitrary = false
  ArbitraryTolerances = false
  EqualTolerance = true
  ExtensionAngle = 0
  FormatSpec = %.2f
  FormatSpecOverTolerance = %+.2f
  FormatSpecUnderTolerance = %+.2f
  Inverted = false
  LineAngle = 0
  LockPosition = false
  MeasureType = 1
  OverTolerance = 0
  References2D = -> [ProjItem008]
  Rotation = 0
  ScaleType = 0
  TheoreticalExact = false
  Type = 2
  UnderTolerance = 0
  X = -60.4902
  Y = 87.8676
FEATURE [TechDraw::DrawViewDimension] Dimension061
  AngleOverride = false
  Arbitrary = false
  ArbitraryTolerances = false
  EqualTolerance = true
  ExtensionAngle = 0
  FormatSpec = ⌀%.2f
  FormatSpecOverTolerance = %+.2f
  FormatSpecUnderTolerance = %+.2f
  Inverted = false
  LineAngle = 0
  LockPosition = false
  MeasureType = 1
  OverTolerance = 0
  References2D = -> [ProjItem008]
  Rotation = 0
  ScaleType = 0
  TheoreticalExact = false
  Type = 5
  UnderTolerance = 0
  X = -5.31668
  Y = 71.4566
FEATURE [TechDraw::DrawViewDimension] Dimension062
  AngleOverride = false
  Arbitrary = false
  ArbitraryTolerances = false
  EqualTolerance = true
  ExtensionAngle = 0
  FormatSpec = ⌀%.2f
  FormatSpecOverTolerance = %+.2f
  FormatSpecUnderTolerance = %+.2f
  Inverted = false
  LineAngle = 0
  LockPosition = false
  MeasureType = 1
  OverTolerance = 0
  References2D = -> [ProjItem008]
  Rotation = 0
  ScaleType = 0
  TheoreticalExact = false
  Type = 5
  UnderTolerance = 0
  X = -13.9297
  Y = -64.9306
FEATURE [TechDraw::DrawPage] Page005
  KeepUpdated = true
  NextBalloonIndex = 1
  ProjectionType = 0
  Template = -> Template005
  Views = -> [ProjGroup005,Dimension055,Dimension056,Dimension057,Dimension058,Dimension059,Dimension060,Dimension061,Dimension062]
FEATURE [TechDraw::DrawSVGTemplate] Template007
  Height = 210
  Orientation = 1
  Width = 297
FEATURE [TechDraw::DrawPage] Page007
  KeepUpdated = true
  NextBalloonIndex = 1
  ProjectionType = 0
  Template = -> Template007
FEATURE [TechDraw::DrawViewDimension] Dimension070
  AngleOverride = false
  Arbitrary = false
  ArbitraryTolerances = false
  EqualTolerance = true
  ExtensionAngle = 0
  FormatSpec = %.2f
  FormatSpecOverTolerance = %+.2f
  FormatSpecUnderTolerance = %+.2f
  Inverted = false
  LineAngle = 0
  LockPosition = false
  MeasureType = 1
  OverTolerance = 0
  References2D = -> [ProjItem003]
  Rotation = 0
  ScaleType = 0
  TheoreticalExact = false
  Type = 1
  UnderTolerance = 0
  X = -15.8384
  Y = 44.865
FEATURE [TechDraw::DrawViewDimension] Dimension071
  AngleOverride = false
  Arbitrary = false
  ArbitraryTolerances = false
  EqualTolerance = true
  ExtensionAngle = 0
  FormatSpec = %.2f
  FormatSpecOverTolerance = %+.2f
  FormatSpecUnderTolerance = %+.2f
  Inverted = false
  LineAngle = 0
  LockPosition = false
  MeasureType = 1
  OverTolerance = 0
  References2D = -> [ProjItem003]
  Rotation = 0
  ScaleType = 0
  TheoreticalExact = false
  Type = 1
  UnderTolerance = 0
  X = -71.9941
  Y = 37.1199
FEATURE [TechDraw::DrawViewDimension] Dimension072
  AngleOverride = false
  Arbitrary = false
  ArbitraryTolerances = false
  EqualTolerance = true
  ExtensionAngle = 0
  FormatSpec = %.2f
  FormatSpecOverTolerance = %+.2f
  FormatSpecUnderTolerance = %+.2f
  Inverted = false
  LineAngle = 0
  LockPosition = false
  MeasureType = 1
  OverTolerance = 0
  References2D = -> [ProjItem003]
  Rotation = 0
  ScaleType = 0
  TheoreticalExact = false
  Type = 2
  UnderTolerance = 0
  X = -87.9346
  Y = 23.293
FEATURE [TechDraw::DrawViewDimension] Dimension073
  AngleOverride = false
  Arbitrary = false
  ArbitraryTolerances = false
  EqualTolerance = true
  ExtensionAngle = 0
  FormatSpec = ⌀%.2f
  FormatSpecOverTolerance = %+.2f
  FormatSpecUnderTolerance = %+.2f
  Inverted = false
  LineAngle = 0
  LockPosition = false
  MeasureType = 1
  OverTolerance = 0
  References2D = -> [ProjItem003]
  Rotation = 0
  ScaleType = 0
  TheoreticalExact = false
  Type = 5
  UnderTolerance = 0
  X = -46.9185
  Y = 31.994
FEATURE [TechDraw::DrawViewDimension] Dimension074
  AngleOverride = false
  Arbitrary = false
  ArbitraryTolerances = false
  EqualTolerance = true
  ExtensionAngle = 0
  FormatSpec = ⌀%.2f
  FormatSpecOverTolerance = %+.2f
  FormatSpecUnderTolerance = %+.2f
  Inverted = false
  LineAngle = 0
  LockPosition = false
  MeasureType = 1
  OverTolerance = 0
  References2D = -> [ProjItem003]
  Rotation = 0
  ScaleType = 0
  TheoreticalExact = false
  Type = 5
  UnderTolerance = 0
  X = -44.597
  Y = 16.8315
FEATURE [TechDraw::DrawViewDimension] Dimension075
  AngleOverride = false
  Arbitrary = false
  ArbitraryTolerances = false
  EqualTolerance = true
  ExtensionAngle = 0
  FormatSpec = %.2f
  FormatSpecOverTolerance = %+.2f
  FormatSpecUnderTolerance = %+.2f
  Inverted = false
  LineAngle = 0
  LockPosition = false
  MeasureType = 1
  OverTolerance = 0
  References2D = -> [ProjItem003]
  Rotation = 0
  ScaleType = 0
  TheoreticalExact = false
  Type = 2
  UnderTolerance = 0
  X = -53.9503
  Y = -16.8534
FEATURE [TechDraw::DrawViewDimension] Dimension076
  AngleOverride = false
  Arbitrary = false
  ArbitraryTolerances = false
  EqualTolerance = true
  ExtensionAngle = 0
  FormatSpec = %.2f
  FormatSpecOverTolerance = %+.2f
  FormatSpecUnderTolerance = %+.2f
  Inverted = false
  LineAngle = 0
  LockPosition = false
  MeasureType = 1
  OverTolerance = 0
  References2D = -> [ProjItem003]
  Rotation = 0
  ScaleType = 0
  TheoreticalExact = false
  Type = 1
  UnderTolerance = 0
  X = -61.4927
  Y = -28.0057
FEATURE [TechDraw::DrawViewDimension] Dimension079
  AngleOverride = false
  Arbitrary = false
  ArbitraryTolerances = false
  EqualTolerance = true
  ExtensionAngle = 0
  FormatSpec = %.2f
  FormatSpecOverTolerance = %+.2f
  FormatSpecUnderTolerance = %+.2f
  Inverted = false
  LineAngle = 0
  LockPosition = false
  MeasureType = 1
  OverTolerance = 0
  References2D = -> [ProjItem003]
  Rotation = 0
  ScaleType = 0
  TheoreticalExact = false
  Type = 2
  UnderTolerance = 0
  X = 79.1614
  Y = 2.61564
FEATURE [TechDraw::DrawViewDimension] Dimension080
  AngleOverride = false
  Arbitrary = false
  ArbitraryTolerances = false
  EqualTolerance = true
  ExtensionAngle = 0
  FormatSpec = %.2f
  FormatSpecOverTolerance = %+.2f
  FormatSpecUnderTolerance = %+.2f
  Inverted = false
  LineAngle = 0
  LockPosition = false
  MeasureType = 1
  OverTolerance = 0
  References2D = -> [ProjItem003]
  Rotation = 0
  ScaleType = 0
  TheoreticalExact = false
  Type = 2
  UnderTolerance = 0
  X = -20.0418
  Y = -0.968942
FEATURE [TechDraw::DrawViewDimension] Dimension081
  AngleOverride = false
  Arbitrary = false
  ArbitraryTolerances = false
  EqualTolerance = true
  ExtensionAngle = 0
  FormatSpec = %.2f
  FormatSpecOverTolerance = %+.2f
  FormatSpecUnderTolerance = %+.2f
  Inverted = false
  LineAngle = 0
  LockPosition = false
  MeasureType = 1
  OverTolerance = 0
  References2D = -> [ProjItem003]
  Rotation = 0
  ScaleType = 0
  TheoreticalExact = false
  Type = 1
  UnderTolerance = 0
  X = -34.314
  Y = -13.4505
FEATURE [TechDraw::DrawPage] Page003  label="DaughterCardDimensions"
  KeepUpdated = true
  NextBalloonIndex = 1
  ProjectionType = 0
  Template = -> Template003
  Views = -> [ProjGroup003,Dimension070,Dimension071,Dimension072,Dimension073,Dimension074,Dimension075,Dimension076,Dimension079,Dimension080,Dimension081]
